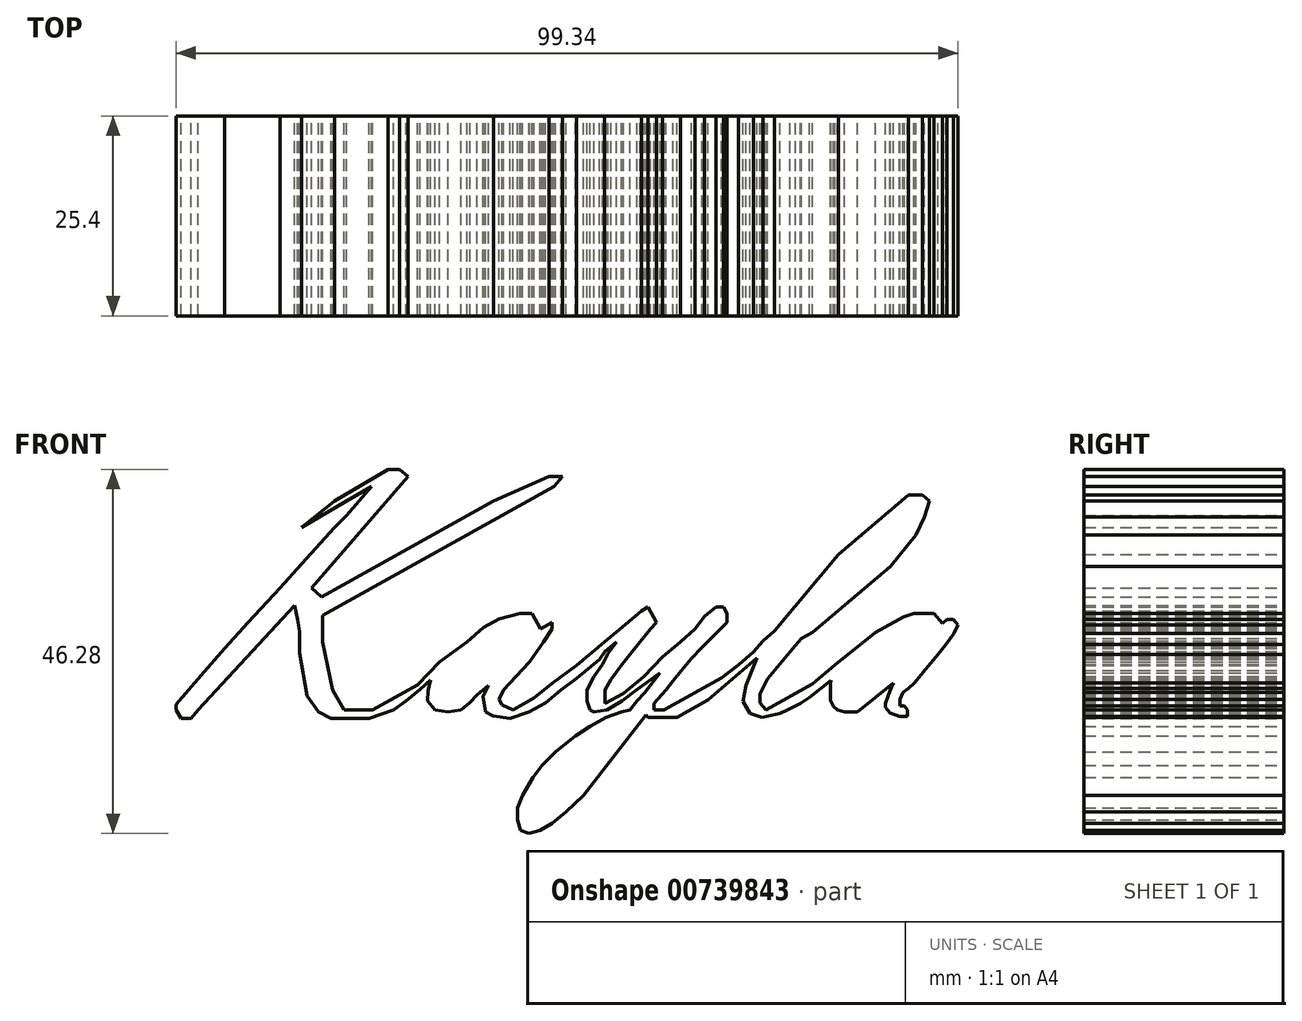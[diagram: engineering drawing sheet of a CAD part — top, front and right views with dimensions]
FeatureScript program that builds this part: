
annotation { "Feature Type Name" : "Feature", "Feature Type Description" : "" }
export const myFeature = defineFeature(function(context is Context, id is Id, definition is map)
    precondition{}
    {
        {
            var Q0;
            Q0=qCreatedBy(makeId("Front.planeOp"),FACE);
            var sketch = newSketch(context, id + "F0", { "sketchPlane" : qUnion([Q0])});
            skLineSegment(sketch, "E0", {"start": v(-52.57, 0.67) * mm, "end": v(-49.39, 4.39) * mm});
            skLineSegment(sketch, "E1", {"start": v(-49.39, 4.39) * mm, "end": v(-46.4, 7.84) * mm});
            skLineSegment(sketch, "E2", {"start": v(-46.4, 7.84) * mm, "end": v(-43.42, 11.09) * mm});
            skLineSegment(sketch, "E3", {"start": v(-43.42, 11.09) * mm, "end": v(-39.37, 15.47) * mm});
            skLineSegment(sketch, "E4", {"start": v(-39.37, 15.47) * mm, "end": v(-36.65, 18.52) * mm});
            skLineSegment(sketch, "E5", {"start": v(-36.65, 18.52) * mm, "end": v(-32.47, 23.16) * mm});
            skLineSegment(sketch, "E6", {"start": v(-32.47, 23.16) * mm, "end": v(-30.94, 24.7) * mm});
            skLineSegment(sketch, "E7", {"start": v(-30.94, 24.7) * mm, "end": v(-27.76, 28.39) * mm});
            skLineSegment(sketch, "E8", {"start": v(-27.76, 28.39) * mm, "end": v(-30.94, 26.54) * mm});
            skPoint(sketch, "E8.endSnap0", {"position": v(-29.35, 26.54) * mm});
            skLineSegment(sketch, "E9", {"start": v(-30.94, 26.54) * mm, "end": v(-36.65, 23.16) * mm});
            skLineSegment(sketch, "E10", {"start": v(-36.65, 23.16) * mm, "end": v(-32.47, 26.54) * mm});
            skLineSegment(sketch, "E11", {"start": v(-32.47, 26.54) * mm, "end": v(-25.67, 30.56) * mm});
            skLineSegment(sketch, "E12", {"start": v(-25.67, 30.56) * mm, "end": v(-24.17, 30.56) * mm});
            skLineSegment(sketch, "E13", {"start": v(-24.17, 30.56) * mm, "end": v(-23.14, 29.67) * mm});
            skLineSegment(sketch, "E14", {"start": v(-23.14, 29.67) * mm, "end": v(-25.83, 26.54) * mm});
            skLineSegment(sketch, "E15", {"start": v(-25.83, 26.54) * mm, "end": v(-30.94, 20.6) * mm});
            skLineSegment(sketch, "E16", {"start": v(-30.94, 20.6) * mm, "end": v(-35.37, 15.47) * mm});
            skLineSegment(sketch, "E17", {"start": v(-35.37, 15.47) * mm, "end": v(-34.1, 14.36) * mm});
            skLineSegment(sketch, "E18", {"start": v(-34.1, 14.36) * mm, "end": v(-12.23, 26.54) * mm});
            skLineSegment(sketch, "E19", {"start": v(-12.23, 26.54) * mm, "end": v(-5.2, 29.67) * mm});
            skLineSegment(sketch, "E20", {"start": v(-5.2, 29.67) * mm, "end": v(-3.47, 29.67) * mm});
            skLineSegment(sketch, "E21", {"start": v(-3.47, 29.67) * mm, "end": v(-4.57, 28.39) * mm});
            skLineSegment(sketch, "E22", {"start": v(-4.57, 28.39) * mm, "end": v(-7.31, 26.86) * mm});
            skLineSegment(sketch, "E23", {"start": v(-7.31, 26.86) * mm, "end": v(-11.56, 24.5) * mm});
            skLineSegment(sketch, "E24", {"start": v(-11.56, 24.5) * mm, "end": v(-15.32, 22.4) * mm});
            skLineSegment(sketch, "E25", {"start": v(-15.32, 22.4) * mm, "end": v(-19.55, 20.05) * mm});
            skLineSegment(sketch, "E26", {"start": v(-19.55, 20.05) * mm, "end": v(-23.14, 18.05) * mm});
            skLineSegment(sketch, "E27", {"start": v(-23.14, 18.05) * mm, "end": v(-29.62, 14.44) * mm});
            skLineSegment(sketch, "E28", {"start": v(-29.62, 14.44) * mm, "end": v(-33.99, 12) * mm});
            skLineSegment(sketch, "E29", {"start": v(-33.99, 12) * mm, "end": v(-33.99, 8.62) * mm});
            skLineSegment(sketch, "E30", {"start": v(-33.99, 8.62) * mm, "end": v(-32.67, 2.51) * mm});
            skLineSegment(sketch, "E31", {"start": v(-32.67, 2.51) * mm, "end": v(-31.27, 0) * mm});
            skLineSegment(sketch, "E32", {"start": v(-31.27, 0) * mm, "end": v(-27.62, 0) * mm});
            skLineSegment(sketch, "E33", {"start": v(-27.62, 0) * mm, "end": v(-21.93, 3.17) * mm});
            skLineSegment(sketch, "E34", {"start": v(-21.93, 3.17) * mm, "end": v(-19.1, 6.07) * mm});
            skLineSegment(sketch, "E35", {"start": v(-19.1, 6.07) * mm, "end": v(-15.64, 8.62) * mm});
            skLineSegment(sketch, "E36", {"start": v(-15.64, 8.62) * mm, "end": v(-13.52, 10.47) * mm});
            skLineSegment(sketch, "E37", {"start": v(-13.52, 10.47) * mm, "end": v(-11.56, 11.57) * mm});
            skLineSegment(sketch, "E38", {"start": v(-11.56, 11.57) * mm, "end": v(-8.9, 12.26) * mm});
            skLineSegment(sketch, "E39", {"start": v(-8.9, 12.26) * mm, "end": v(-7.39, 12.26) * mm});
            skLineSegment(sketch, "E40", {"start": v(-7.39, 12.26) * mm, "end": v(-6.93, 11.45) * mm});
            skLineSegment(sketch, "E41", {"start": v(-6.93, 11.45) * mm, "end": v(-6.3, 10.3) * mm});
            skLineSegment(sketch, "E42", {"start": v(-6.3, 10.3) * mm, "end": v(-5.35, 10.84) * mm});
            skLineSegment(sketch, "E43", {"start": v(-5.35, 10.84) * mm, "end": v(-4.84, 11.12) * mm});
            skLineSegment(sketch, "E44", {"start": v(-4.84, 11.12) * mm, "end": v(-4.84, 10.3) * mm});
            skLineSegment(sketch, "E45", {"start": v(-4.84, 10.3) * mm, "end": v(-5.88, 8.62) * mm});
            skLineSegment(sketch, "E46", {"start": v(-5.88, 8.62) * mm, "end": v(-7.67, 6.12) * mm});
            skLineSegment(sketch, "E47", {"start": v(-7.67, 6.12) * mm, "end": v(-9.4, 4.23) * mm});
            skLineSegment(sketch, "E48", {"start": v(-9.4, 4.23) * mm, "end": v(-10.96, 2.51) * mm});
            skLineSegment(sketch, "E49", {"start": v(-10.96, 2.51) * mm, "end": v(-11.56, 1.32) * mm});
            skLineSegment(sketch, "E50", {"start": v(-11.56, 1.32) * mm, "end": v(-11.18, 0.64) * mm});
            skLineSegment(sketch, "E51", {"start": v(-11.18, 0.64) * mm, "end": v(-9.79, 0) * mm});
            skLineSegment(sketch, "E52", {"start": v(-9.79, 0) * mm, "end": v(-7.11, 1.49) * mm});
            skLineSegment(sketch, "E53", {"start": v(-7.11, 1.49) * mm, "end": v(-4.84, 3.39) * mm});
            skLineSegment(sketch, "E54", {"start": v(-4.84, 3.39) * mm, "end": v(-1.7, 5.68) * mm});
            skLineSegment(sketch, "E55", {"start": v(-1.7, 5.68) * mm, "end": v(1.87, 8.62) * mm});
            skLineSegment(sketch, "E56", {"start": v(1.87, 8.62) * mm, "end": v(4.5, 10.84) * mm});
            skLineSegment(sketch, "E57", {"start": v(4.5, 10.84) * mm, "end": v(6.56, 12.6) * mm});
            skLineSegment(sketch, "E58", {"start": v(6.56, 12.6) * mm, "end": v(7.38, 13.05) * mm});
            skLineSegment(sketch, "E59", {"start": v(7.38, 13.05) * mm, "end": v(7.7, 12.5) * mm});
            skLineSegment(sketch, "E60", {"start": v(7.7, 12.5) * mm, "end": v(8.07, 11.8) * mm});
            skLineSegment(sketch, "E61", {"start": v(8.07, 11.8) * mm, "end": v(8.46, 11.12) * mm});
            skLineSegment(sketch, "E62", {"start": v(8.46, 11.12) * mm, "end": v(7.7, 10.3) * mm});
            skLineSegment(sketch, "E63", {"start": v(7.7, 10.3) * mm, "end": v(6.34, 8.62) * mm});
            skLineSegment(sketch, "E64", {"start": v(6.34, 8.62) * mm, "end": v(5.05, 7.07) * mm});
            skLineSegment(sketch, "E65", {"start": v(5.05, 7.07) * mm, "end": v(4.05, 5.79) * mm});
            skLineSegment(sketch, "E66", {"start": v(4.05, 5.79) * mm, "end": v(2.66, 3.9) * mm});
            skLineSegment(sketch, "E67", {"start": v(2.66, 3.9) * mm, "end": v(1.93, 2.51) * mm});
            skLineSegment(sketch, "E68", {"start": v(1.93, 2.51) * mm, "end": v(1.93, 1.66) * mm});
            skLineSegment(sketch, "E69", {"start": v(1.93, 1.66) * mm, "end": v(1.93, 0.82) * mm});
            skLineSegment(sketch, "E70", {"start": v(1.93, 0.82) * mm, "end": v(4.24, 2.1) * mm});
            skLineSegment(sketch, "E71", {"start": v(4.24, 2.1) * mm, "end": v(6.84, 4.28) * mm});
            skLineSegment(sketch, "E72", {"start": v(6.84, 4.28) * mm, "end": v(9.18, 6.74) * mm});
            skLineSegment(sketch, "E73", {"start": v(9.18, 6.74) * mm, "end": v(11.53, 8.62) * mm});
            skLineSegment(sketch, "E74", {"start": v(11.53, 8.62) * mm, "end": v(13.31, 10.3) * mm});
            skLineSegment(sketch, "E75", {"start": v(13.31, 10.3) * mm, "end": v(14.54, 11.87) * mm});
            skLineSegment(sketch, "E76", {"start": v(14.54, 11.87) * mm, "end": v(16, 13.05) * mm});
            skLineSegment(sketch, "E77", {"start": v(16, 13.05) * mm, "end": v(16.94, 13.05) * mm});
            skLineSegment(sketch, "E78", {"start": v(16.94, 13.05) * mm, "end": v(17.39, 12.26) * mm});
            skLineSegment(sketch, "E79", {"start": v(17.39, 12.26) * mm, "end": v(17.39, 11.12) * mm});
            skLineSegment(sketch, "E80", {"start": v(17.39, 11.12) * mm, "end": v(14.2, 7.96) * mm});
            skLineSegment(sketch, "E81", {"start": v(14.2, 7.96) * mm, "end": v(12.92, 6.51) * mm});
            skLineSegment(sketch, "E82", {"start": v(12.92, 6.51) * mm, "end": v(11.64, 5) * mm});
            skLineSegment(sketch, "E83", {"start": v(11.64, 5) * mm, "end": v(10.58, 3.67) * mm});
            skLineSegment(sketch, "E84", {"start": v(10.58, 3.67) * mm, "end": v(9.69, 2.51) * mm});
            skLineSegment(sketch, "E85", {"start": v(9.69, 2.51) * mm, "end": v(8.12, 0.82) * mm});
            skLineSegment(sketch, "E86", {"start": v(8.12, 0.82) * mm, "end": v(8.12, 0) * mm});
            skLineSegment(sketch, "E87", {"start": v(8.12, 0) * mm, "end": v(9.4, 0) * mm});
            skLineSegment(sketch, "E88", {"start": v(9.4, 0) * mm, "end": v(11.18, 0.99) * mm});
            skLineSegment(sketch, "E89", {"start": v(11.18, 0.99) * mm, "end": v(13.92, 2.51) * mm});
            skLineSegment(sketch, "E90", {"start": v(13.92, 2.51) * mm, "end": v(16.72, 4.07) * mm});
            skLineSegment(sketch, "E91", {"start": v(16.72, 4.07) * mm, "end": v(18.84, 5.73) * mm});
            skLineSegment(sketch, "E92", {"start": v(18.84, 5.73) * mm, "end": v(20.74, 7.35) * mm});
            skLineSegment(sketch, "E93", {"start": v(20.74, 7.35) * mm, "end": v(21.98, 8.75) * mm});
            skLineSegment(sketch, "E94", {"start": v(21.98, 8.75) * mm, "end": v(23.45, 10) * mm});
            skLineSegment(sketch, "E95", {"start": v(23.45, 10) * mm, "end": v(24.66, 11.45) * mm});
            skLineSegment(sketch, "E96", {"start": v(24.66, 11.45) * mm, "end": v(26.1, 13.18) * mm});
            skLineSegment(sketch, "E97", {"start": v(26.1, 13.18) * mm, "end": v(28.27, 15.8) * mm});
            skLineSegment(sketch, "E98", {"start": v(28.27, 15.8) * mm, "end": v(29.81, 17.66) * mm});
            skLineSegment(sketch, "E99", {"start": v(29.81, 17.66) * mm, "end": v(31.57, 19.77) * mm});
            skLineSegment(sketch, "E100", {"start": v(31.57, 19.77) * mm, "end": v(33.52, 21.43) * mm});
            skLineSegment(sketch, "E101", {"start": v(33.52, 21.43) * mm, "end": v(35.36, 22.99) * mm});
            skLineSegment(sketch, "E102", {"start": v(35.36, 22.99) * mm, "end": v(37.14, 24.5) * mm});
            skLineSegment(sketch, "E103", {"start": v(37.14, 24.5) * mm, "end": v(39.16, 26.2) * mm});
            skLineSegment(sketch, "E104", {"start": v(39.16, 26.2) * mm, "end": v(40.43, 27.29) * mm});
            skLineSegment(sketch, "E105", {"start": v(40.43, 27.29) * mm, "end": v(42.23, 27.29) * mm});
            skLineSegment(sketch, "E106", {"start": v(42.23, 27.29) * mm, "end": v(43.1, 26.57) * mm});
            skLineSegment(sketch, "E107", {"start": v(43.1, 26.57) * mm, "end": v(42.5, 24.5) * mm});
            skLineSegment(sketch, "E108", {"start": v(42.5, 24.5) * mm, "end": v(41.44, 22.2) * mm});
            skLineSegment(sketch, "E109", {"start": v(41.44, 22.2) * mm, "end": v(39.66, 20.06) * mm});
            skLineSegment(sketch, "E110", {"start": v(39.66, 20.06) * mm, "end": v(38.14, 18.23) * mm});
            skLineSegment(sketch, "E111", {"start": v(38.14, 18.23) * mm, "end": v(35.7, 16.16) * mm});
            skLineSegment(sketch, "E112", {"start": v(35.7, 16.16) * mm, "end": v(33.67, 14.44) * mm});
            skLineSegment(sketch, "E113", {"start": v(33.67, 14.44) * mm, "end": v(30.97, 12.15) * mm});
            skLineSegment(sketch, "E114", {"start": v(30.97, 12.15) * mm, "end": v(28.27, 9.86) * mm});
            skLineSegment(sketch, "E115", {"start": v(28.27, 9.86) * mm, "end": v(26.85, 9.07) * mm});
            skLineSegment(sketch, "E116", {"start": v(26.85, 9.07) * mm, "end": v(26.1, 8.16) * mm});
            skLineSegment(sketch, "E117", {"start": v(26.1, 8.16) * mm, "end": v(25.38, 7.35) * mm});
            skLineSegment(sketch, "E118", {"start": v(25.38, 7.35) * mm, "end": v(24.04, 5.73) * mm});
            skLineSegment(sketch, "E119", {"start": v(24.04, 5.73) * mm, "end": v(22.57, 3.96) * mm});
            skLineSegment(sketch, "E120", {"start": v(22.57, 3.96) * mm, "end": v(21.6, 2.03) * mm});
            skLineSegment(sketch, "E121", {"start": v(21.6, 2.03) * mm, "end": v(21.6, 0.9) * mm});
            skLineSegment(sketch, "E122", {"start": v(21.6, 0.9) * mm, "end": v(22.36, 0) * mm});
            skLineSegment(sketch, "E123", {"start": v(22.36, 0) * mm, "end": v(24.15, 1) * mm});
            skLineSegment(sketch, "E124", {"start": v(24.15, 1) * mm, "end": v(26.1, 2.08) * mm});
            skLineSegment(sketch, "E125", {"start": v(26.1, 2.08) * mm, "end": v(28.27, 3.3) * mm});
            skLineSegment(sketch, "E126", {"start": v(28.27, 3.3) * mm, "end": v(31.15, 5.73) * mm});
            skLineSegment(sketch, "E127", {"start": v(31.15, 5.73) * mm, "end": v(33.16, 7.35) * mm});
            skLineSegment(sketch, "E128", {"start": v(33.16, 7.35) * mm, "end": v(36.29, 9.86) * mm});
            skLineSegment(sketch, "E129", {"start": v(36.29, 9.86) * mm, "end": v(38.05, 10.84) * mm});
            skLineSegment(sketch, "E130", {"start": v(38.05, 10.84) * mm, "end": v(39.81, 11.82) * mm});
            skLineSegment(sketch, "E131", {"start": v(39.81, 11.82) * mm, "end": v(41.17, 12.25) * mm});
            skLineSegment(sketch, "E132", {"start": v(41.17, 12.25) * mm, "end": v(42.37, 12.25) * mm});
            skLineSegment(sketch, "E133", {"start": v(42.37, 12.25) * mm, "end": v(43.7, 12.25) * mm});
            skLineSegment(sketch, "E134", {"start": v(43.7, 12.25) * mm, "end": v(44.37, 11.45) * mm});
            skLineSegment(sketch, "E135", {"start": v(44.37, 11.45) * mm, "end": v(44.77, 10.98) * mm});
            skLineSegment(sketch, "E136", {"start": v(44.77, 10.98) * mm, "end": v(45.35, 11.48) * mm});
            skLineSegment(sketch, "E137", {"start": v(45.35, 11.48) * mm, "end": v(46.18, 11.48) * mm});
            skLineSegment(sketch, "E138", {"start": v(46.18, 11.48) * mm, "end": v(46.77, 10.78) * mm});
            skLineSegment(sketch, "E139", {"start": v(46.77, 10.78) * mm, "end": v(46.21, 9.7) * mm});
            skLineSegment(sketch, "E140", {"start": v(46.21, 9.7) * mm, "end": v(45.22, 8.33) * mm});
            skLineSegment(sketch, "E141", {"start": v(45.22, 8.33) * mm, "end": v(44.22, 7.07) * mm});
            skLineSegment(sketch, "E142", {"start": v(44.22, 7.07) * mm, "end": v(42.4, 4.83) * mm});
            skLineSegment(sketch, "E143", {"start": v(42.4, 4.83) * mm, "end": v(41.2, 3.41) * mm});
            skLineSegment(sketch, "E144", {"start": v(41.2, 3.41) * mm, "end": v(40.43, 2.75) * mm});
            skLineSegment(sketch, "E145", {"start": v(40.43, 2.75) * mm, "end": v(39.78, 2.24) * mm});
            skLineSegment(sketch, "E146", {"start": v(39.78, 2.24) * mm, "end": v(39.35, 1.32) * mm});
            skLineSegment(sketch, "E147", {"start": v(39.35, 1.32) * mm, "end": v(39.35, 0.5) * mm});
            skLineSegment(sketch, "E148", {"start": v(39.35, 0.5) * mm, "end": v(39.94, 0.5) * mm});
            skLineSegment(sketch, "E149", {"start": v(39.94, 0.5) * mm, "end": v(40.34, 0) * mm});
            skLineSegment(sketch, "E150", {"start": v(40.34, 0) * mm, "end": v(40.34, -0.85) * mm});
            skLineSegment(sketch, "E151", {"start": v(40.34, -0.85) * mm, "end": v(39.31, -0.85) * mm});
            skLineSegment(sketch, "E152", {"start": v(39.31, -0.85) * mm, "end": v(38.09, -0.37) * mm});
            skLineSegment(sketch, "E153", {"start": v(38.09, -0.37) * mm, "end": v(37.55, 0.3) * mm});
            skLineSegment(sketch, "E154", {"start": v(37.55, 0.3) * mm, "end": v(37.55, 0.85) * mm});
            skLineSegment(sketch, "E155", {"start": v(37.55, 0.85) * mm, "end": v(37.85, 1.68) * mm});
            skLineSegment(sketch, "E156", {"start": v(37.85, 1.68) * mm, "end": v(38.13, 2.43) * mm});
            skLineSegment(sketch, "E157", {"start": v(38.13, 2.43) * mm, "end": v(38.56, 3.41) * mm});
            skLineSegment(sketch, "E158", {"start": v(38.56, 3.41) * mm, "end": v(37.74, 2.75) * mm});
            skLineSegment(sketch, "E159", {"start": v(37.74, 2.75) * mm, "end": v(36.9, 2.07) * mm});
            skLineSegment(sketch, "E160", {"start": v(36.9, 2.07) * mm, "end": v(35.76, 1.16) * mm});
            skLineSegment(sketch, "E161", {"start": v(35.76, 1.16) * mm, "end": v(34.93, 0.5) * mm});
            skLineSegment(sketch, "E162", {"start": v(34.93, 0.5) * mm, "end": v(33.96, -0.28) * mm});
            skLineSegment(sketch, "E163", {"start": v(33.96, -0.28) * mm, "end": v(32.33, -0.28) * mm});
            skLineSegment(sketch, "E164", {"start": v(32.33, -0.28) * mm, "end": v(31.46, 0) * mm});
            skLineSegment(sketch, "E165", {"start": v(31.46, 0) * mm, "end": v(30.95, 0.45) * mm});
            skLineSegment(sketch, "E166", {"start": v(30.95, 0.45) * mm, "end": v(30.54, 1.2) * mm});
            skLineSegment(sketch, "E167", {"start": v(30.54, 1.2) * mm, "end": v(30.54, 1.64) * mm});
            skLineSegment(sketch, "E168", {"start": v(30.54, 1.64) * mm, "end": v(30.54, 2.66) * mm});
            skLineSegment(sketch, "E169", {"start": v(30.54, 2.66) * mm, "end": v(30.55, 3.26) * mm});
            skLineSegment(sketch, "E170", {"start": v(30.55, 3.26) * mm, "end": v(30.6, 3.73) * mm});
            skLineSegment(sketch, "E171", {"start": v(27.91, 1.6) * mm, "end": v(30.6, 3.73) * mm});
            skLineSegment(sketch, "E172", {"start": v(27.91, 1.6) * mm, "end": v(26.73, 0.81) * mm});
            skLineSegment(sketch, "E173", {"start": v(26.73, 0.81) * mm, "end": v(25.07, 0) * mm});
            skLineSegment(sketch, "E174", {"start": v(25.07, 0) * mm, "end": v(24.12, -0.45) * mm});
            skLineSegment(sketch, "E175", {"start": v(21.84, -0.93) * mm, "end": v(24.12, -0.45) * mm});
            skLineSegment(sketch, "E176", {"start": v(20.3, -0.45) * mm, "end": v(19.45, 1.07) * mm});
            skLineSegment(sketch, "E177", {"start": v(19.45, 1.07) * mm, "end": v(19.82, 3.14) * mm});
            skLineSegment(sketch, "E178", {"start": v(21.84, -0.93) * mm, "end": v(20.3, -0.45) * mm});
            skLineSegment(sketch, "E179", {"start": v(19.82, 3.14) * mm, "end": v(21.24, 6.57) * mm});
            skLineSegment(sketch, "E180", {"start": v(21.24, 6.57) * mm, "end": v(20.58, 6.01) * mm});
            skLineSegment(sketch, "E181", {"start": v(20.58, 6.01) * mm, "end": v(19.82, 5.37) * mm});
            skLineSegment(sketch, "E182", {"start": v(19.82, 5.37) * mm, "end": v(19.22, 4.85) * mm});
            skLineSegment(sketch, "E183", {"start": v(19.22, 4.85) * mm, "end": v(18.13, 3.93) * mm});
            skLineSegment(sketch, "E184", {"start": v(18.13, 3.93) * mm, "end": v(17.2, 3.14) * mm});
            skLineSegment(sketch, "E185", {"start": v(17.2, 3.14) * mm, "end": v(16.04, 2.16) * mm});
            skLineSegment(sketch, "E186", {"start": v(16.04, 2.16) * mm, "end": v(15.02, 1.29) * mm});
            skLineSegment(sketch, "E187", {"start": v(15.02, 1.29) * mm, "end": v(12.7, 0) * mm});
            skLineSegment(sketch, "E188", {"start": v(12.7, 0) * mm, "end": v(11.04, -0.93) * mm});
            skLineSegment(sketch, "E189", {"start": v(11.04, -0.93) * mm, "end": v(9.17, -0.93) * mm});
            skLineSegment(sketch, "E190", {"start": v(9.17, -0.93) * mm, "end": v(7.36, -0.93) * mm});
            skLineSegment(sketch, "E191", {"start": v(7.36, -0.93) * mm, "end": v(7.13, -0.66) * mm});
            skLineSegment(sketch, "E192", {"start": v(7.13, -0.66) * mm, "end": v(6.57, -1.38) * mm});
            skLineSegment(sketch, "E193", {"start": v(6.57, -1.38) * mm, "end": v(5.95, -2.18) * mm});
            skLineSegment(sketch, "E194", {"start": v(5.95, -2.18) * mm, "end": v(5.34, -2.95) * mm});
            skLineSegment(sketch, "E195", {"start": v(5.34, -2.95) * mm, "end": v(4.54, -3.98) * mm});
            skLineSegment(sketch, "E196", {"start": v(4.54, -3.98) * mm, "end": v(4.08, -4.56) * mm});
            skLineSegment(sketch, "E197", {"start": v(4.08, -4.56) * mm, "end": v(2.75, -6.26) * mm});
            skLineSegment(sketch, "E198", {"start": v(2.75, -6.26) * mm, "end": v(1.35, -8.06) * mm});
            skLineSegment(sketch, "E199", {"start": v(1.35, -8.06) * mm, "end": v(0.21, -9.5) * mm});
            skLineSegment(sketch, "E200", {"start": v(0.21, -9.5) * mm, "end": v(-0.83, -10.84) * mm});
            skLineSegment(sketch, "E201", {"start": v(-3.05, -12.96) * mm, "end": v(-0.83, -10.84) * mm});
            skLineSegment(sketch, "E202", {"start": v(-3.05, -12.96) * mm, "end": v(-4.84, -14.42) * mm});
            skLineSegment(sketch, "E203", {"start": v(-4.84, -14.42) * mm, "end": v(-6.34, -15.28) * mm});
            skLineSegment(sketch, "E204", {"start": v(-6.34, -15.28) * mm, "end": v(-7.76, -15.72) * mm});
            skLineSegment(sketch, "E205", {"start": v(-7.76, -15.72) * mm, "end": v(-8.82, -15.28) * mm});
            skLineSegment(sketch, "E206", {"start": v(-8.82, -15.28) * mm, "end": v(-9.22, -14) * mm});
            skLineSegment(sketch, "E207", {"start": v(-9.22, -14) * mm, "end": v(-9.22, -12.46) * mm});
            skLineSegment(sketch, "E208", {"start": v(-9.22, -12.46) * mm, "end": v(-8.56, -10.84) * mm});
            skLineSegment(sketch, "E209", {"start": v(-8.56, -10.84) * mm, "end": v(-7.27, -8.58) * mm});
            skLineSegment(sketch, "E210", {"start": v(-7.27, -8.58) * mm, "end": v(-6.08, -7.07) * mm});
            skLineSegment(sketch, "E211", {"start": v(-6.08, -7.07) * mm, "end": v(-4.38, -5.33) * mm});
            skLineSegment(sketch, "E212", {"start": v(-4.38, -5.33) * mm, "end": v(-3.38, -4.54) * mm});
            skLineSegment(sketch, "E213", {"start": v(-3.38, -4.54) * mm, "end": v(-1.82, -3.3) * mm});
            skLineSegment(sketch, "E214", {"start": v(-1.82, -3.3) * mm, "end": v(0, -2.08) * mm});
            skLineSegment(sketch, "E215", {"start": v(0, -2.08) * mm, "end": v(2.02, -0.95) * mm});
            skLineSegment(sketch, "E216", {"start": v(2.02, -0.95) * mm, "end": v(3.98, -0.29) * mm});
            skLineSegment(sketch, "E217", {"start": v(3.98, -0.29) * mm, "end": v(5.1, 0) * mm});
            skLineSegment(sketch, "E218", {"start": v(5.1, 0) * mm, "end": v(6, 1.16) * mm});
            skLineSegment(sketch, "E219", {"start": v(6, 1.16) * mm, "end": v(6.93, 2.16) * mm});
            skLineSegment(sketch, "E220", {"start": v(6.93, 2.16) * mm, "end": v(8.9, 4.69) * mm});
            skPoint(sketch, "E220.endSnap0", {"position": v(8.9, 1.67) * mm});
            skLineSegment(sketch, "E221", {"start": v(8.9, 4.69) * mm, "end": v(7.8, 3.9) * mm});
            skLineSegment(sketch, "E222", {"start": v(7.8, 3.9) * mm, "end": v(5.9, 2.51) * mm});
            skLineSegment(sketch, "E223", {"start": v(5.9, 2.51) * mm, "end": v(4.07, 1.16) * mm});
            skLineSegment(sketch, "E224", {"start": v(2.15, 0) * mm, "end": v(4.07, 1.16) * mm});
            skLineSegment(sketch, "E225", {"start": v(0.5, -0.29) * mm, "end": v(2.15, 0) * mm});
            skLineSegment(sketch, "E226", {"start": v(0.5, -0.29) * mm, "end": v(0, 0) * mm});
            skLineSegment(sketch, "E227", {"start": v(0, 0) * mm, "end": v(-0.4, 1.16) * mm});
            skLineSegment(sketch, "E228", {"start": v(-0.4, 1.16) * mm, "end": v(-0.4, 2.51) * mm});
            skLineSegment(sketch, "E229", {"start": v(-0.4, 2.51) * mm, "end": v(0.05, 3.39) * mm});
            skLineSegment(sketch, "E230", {"start": v(0.05, 3.39) * mm, "end": v(0.5, 4.27) * mm});
            skLineSegment(sketch, "E231", {"start": v(0.5, 4.27) * mm, "end": v(1.61, 5.79) * mm});
            skLineSegment(sketch, "E232", {"start": v(1.61, 5.79) * mm, "end": v(2.32, 7.18) * mm});
            skLineSegment(sketch, "E233", {"start": v(2.32, 7.18) * mm, "end": v(3.37, 8.62) * mm});
            skLineSegment(sketch, "E234", {"start": v(3.37, 8.62) * mm, "end": v(1.93, 7.41) * mm});
            skLineSegment(sketch, "E235", {"start": v(1.93, 7.41) * mm, "end": v(1.2, 6.42) * mm});
            skLineSegment(sketch, "E236", {"start": v(1.2, 6.42) * mm, "end": v(0, 5.41) * mm});
            skLineSegment(sketch, "E237", {"start": v(0, 5.41) * mm, "end": v(-1.72, 3.97) * mm});
            skLineSegment(sketch, "E238", {"start": v(-1.72, 3.97) * mm, "end": v(-3.7, 2.51) * mm});
            skLineSegment(sketch, "E239", {"start": v(-3.7, 2.51) * mm, "end": v(-5.67, 0.87) * mm});
            skLineSegment(sketch, "E240", {"start": v(-5.67, 0.87) * mm, "end": v(-7.74, -0.29) * mm});
            skLineSegment(sketch, "E241", {"start": v(-7.74, -0.29) * mm, "end": v(-10.16, -1.1) * mm});
            skLineSegment(sketch, "E242", {"start": v(-10.16, -1.1) * mm, "end": v(-12.33, -0.76) * mm});
            skLineSegment(sketch, "E243", {"start": v(-12.33, -0.76) * mm, "end": v(-13.26, -0.29) * mm});
            skLineSegment(sketch, "E244", {"start": v(-13.26, -0.29) * mm, "end": v(-13.51, 1.16) * mm});
            skLineSegment(sketch, "E245", {"start": v(-13.51, 1.16) * mm, "end": v(-13.6, 1.68) * mm});
            skLineSegment(sketch, "E246", {"start": v(-13.6, 1.68) * mm, "end": v(-12.87, 3.12) * mm});
            skLineSegment(sketch, "E247", {"start": v(-12.87, 3.12) * mm, "end": v(-14.32, 1.91) * mm});
            skLineSegment(sketch, "E248", {"start": v(-14.32, 1.91) * mm, "end": v(-15.24, 0.93) * mm});
            skLineSegment(sketch, "E249", {"start": v(-15.24, 0.93) * mm, "end": v(-16.36, 0) * mm});
            skLineSegment(sketch, "E250", {"start": v(-16.36, 0) * mm, "end": v(-18.02, -0.29) * mm});
            skLineSegment(sketch, "E251", {"start": v(-18.02, -0.29) * mm, "end": v(-19.66, 0) * mm});
            skLineSegment(sketch, "E252", {"start": v(-19.66, 0) * mm, "end": v(-20.63, 1.16) * mm});
            skLineSegment(sketch, "E253", {"start": v(-20.63, 1.16) * mm, "end": v(-20.57, 2.43) * mm});
            skLineSegment(sketch, "E254", {"start": v(-20.57, 2.43) * mm, "end": v(-20.26, 3.81) * mm});
            skLineSegment(sketch, "E255", {"start": v(-20.26, 3.81) * mm, "end": v(-21.6, 2.63) * mm});
            skLineSegment(sketch, "E256", {"start": v(-21.6, 2.63) * mm, "end": v(-23.36, 1.16) * mm});
            skLineSegment(sketch, "E257", {"start": v(-23.36, 1.16) * mm, "end": v(-24.93, 0) * mm});
            skLineSegment(sketch, "E258", {"start": v(-24.93, 0) * mm, "end": v(-26.77, -0.63) * mm});
            skLineSegment(sketch, "E259", {"start": v(-26.77, -0.63) * mm, "end": v(-28.07, -1.07) * mm});
            skLineSegment(sketch, "E260", {"start": v(-28.07, -1.07) * mm, "end": v(-30.2, -1.07) * mm});
            skLineSegment(sketch, "E261", {"start": v(-30.2, -1.07) * mm, "end": v(-32.92, -1.07) * mm});
            skLineSegment(sketch, "E262", {"start": v(-32.92, -1.07) * mm, "end": v(-34.46, -0.29) * mm});
            skLineSegment(sketch, "E263", {"start": v(-34.46, -0.29) * mm, "end": v(-35.96, 1.74) * mm});
            skLineSegment(sketch, "E264", {"start": v(-35.96, 1.74) * mm, "end": v(-36.51, 4.93) * mm});
            skLineSegment(sketch, "E265", {"start": v(-36.51, 4.93) * mm, "end": v(-36.91, 7.25) * mm});
            skLineSegment(sketch, "E266", {"start": v(-36.91, 7.25) * mm, "end": v(-36.91, 9.97) * mm});
            skLineSegment(sketch, "E267", {"start": v(-36.91, 9.97) * mm, "end": v(-37.14, 11.48) * mm});
            skLineSegment(sketch, "E268", {"start": v(-37.14, 11.48) * mm, "end": v(-37.5, 13.28) * mm});
            skPoint(sketch, "E268.endSnap0", {"position": v(-41.4, 13.28) * mm});
            skLineSegment(sketch, "E269", {"start": v(-37.5, 13.28) * mm, "end": v(-39.44, 11.19) * mm});
            skLineSegment(sketch, "E270", {"start": v(-39.44, 11.19) * mm, "end": v(-41.05, 9.44) * mm});
            skLineSegment(sketch, "E271", {"start": v(-41.05, 9.44) * mm, "end": v(-43.02, 7.3) * mm});
            skLineSegment(sketch, "E272", {"start": v(-43.02, 7.3) * mm, "end": v(-45.09, 5.07) * mm});
            skLineSegment(sketch, "E273", {"start": v(-45.09, 5.07) * mm, "end": v(-46.68, 3.35) * mm});
            skLineSegment(sketch, "E274", {"start": v(-46.68, 3.35) * mm, "end": v(-48.27, 1.63) * mm});
            skLineSegment(sketch, "E275", {"start": v(-48.27, 1.63) * mm, "end": v(-49.78, 0) * mm});
            skLineSegment(sketch, "E276", {"start": v(-49.78, 0) * mm, "end": v(-50.65, -1.1) * mm});
            skLineSegment(sketch, "E277", {"start": v(-52.57, 0.67) * mm, "end": v(-52.57, 0) * mm});
            skLineSegment(sketch, "E278", {"start": v(-52.57, 0) * mm, "end": v(-51.97, -1.06) * mm});
            skLineSegment(sketch, "E279", {"start": v(-51.97, -1.06) * mm, "end": v(-50.65, -1.1) * mm});
            skSolve(sketch);
        }
        {
            var Q0;
            Q0=makeQuery(id+"F0.imprint","IMPRINT",FACE,{"disambiguationData":[TD([[makeQuery(id+"F0.imprint","IMPRINT",EDGE,{"derivedFrom":sQuery(id+"F0.wireOp",EDGE,"E0")}),-1.0]])]});
            extrude(context, id + "F1", {"entities" : qUnion([Q0]), "depth" : 25.4 * mm, "offsetDistance" : 25.4 * mm});
        }
    });
